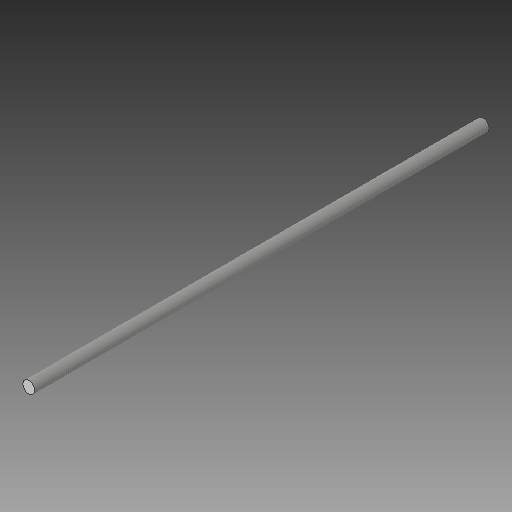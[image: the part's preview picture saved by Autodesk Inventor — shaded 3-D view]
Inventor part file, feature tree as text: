
AUTODESK INVENTOR PART (.ipt)
format: ipt  version: 2018 (Build 220112000, 112)  size: 93,184 bytes
history: native  units: mm
features: other x1, extrude x1, thread x1, sketch x1
ambient origin geometry x8: Origin, YZ Plane, XZ Plane, XY Plane, X Axis, Y Axis, Z Axis, Center Point
bodies: Body1 (feature_tree)
feature tree (4):
  other  "ソリッド1"
  extrude  "押し出し1"  Depth=10.0mm
  thread  "ねじ1"
  sketch  "スケッチ1"
